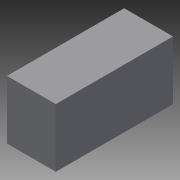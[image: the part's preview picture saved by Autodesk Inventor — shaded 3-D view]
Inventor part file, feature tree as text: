
AUTODESK INVENTOR PART (.ipt)
format: ipt  version: 2014 (Build 180170000, 170)  size: 69,120 bytes
history: native  units: in
note: dims shown in document units (in); Inventor stores cm internally (conversion verified against a paired STEP export)
features: extrude x1, sketch x1
ambient origin geometry x8: Origin, YZ Plane, XZ Plane, XY Plane, X Axis, Y Axis, Z Axis, Center Point
bodies: Solid1 (feature_tree)
feature tree (2):
  extrude  "Extrusion1"  Depth=72.0in
  sketch  "Sketch1"  dims[d0=30.0in d1=72.0in d2=30.0in d3=0.0in]
